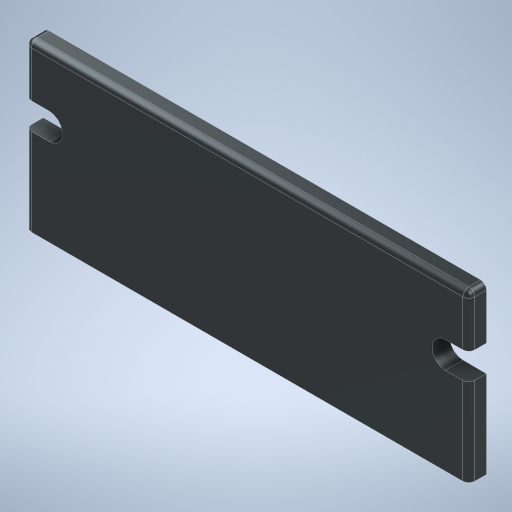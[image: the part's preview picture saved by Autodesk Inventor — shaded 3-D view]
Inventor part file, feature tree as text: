
AUTODESK INVENTOR PART (.ipt)
format: ipt  version: 2023 (Build 270158000, 158)  size: 280,064 bytes
history: native  units: mm
features: extrude x1, fillet x1, sketch x1
ambient origin geometry x8: Origin, YZ Plane, XZ Plane, XY Plane, X Axis, Y Axis, Z Axis, Center Point
bodies: Solid1 (feature_tree)
feature tree (3):
  extrude  "Extrusion1"  Depth=28.0mm
  fillet  "Fillet1"  Radius=11.0mm
  sketch  "Sketch1"  dims[d0=75.0mm d1=28.0mm d2=11.0mm d3=4.0mm d4=4.5mm d5=3.0mm d6=0.0mm d7=1.0mm]
